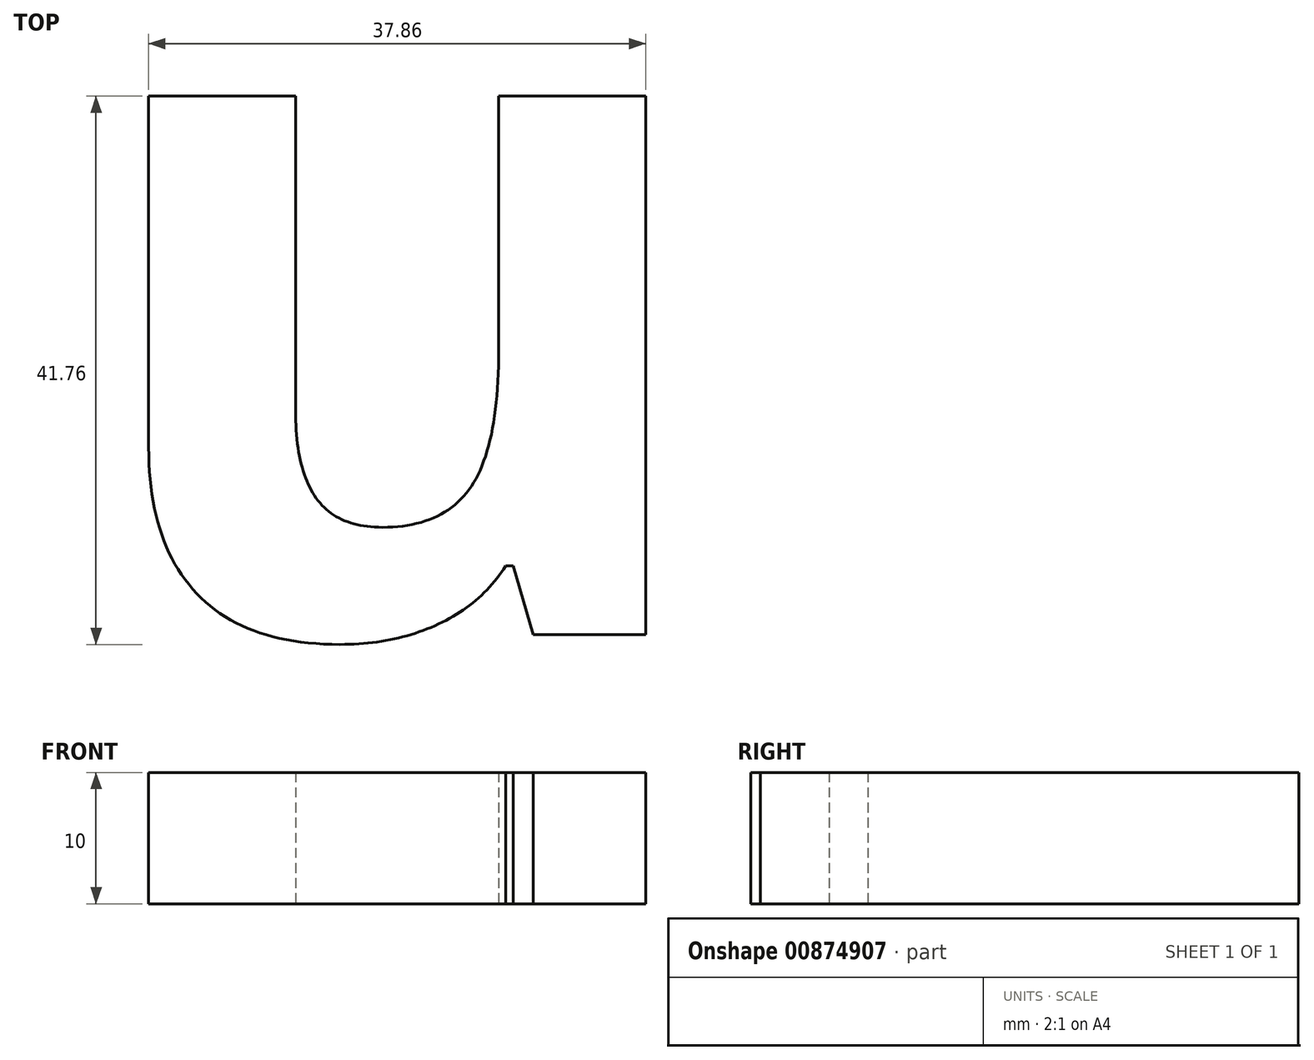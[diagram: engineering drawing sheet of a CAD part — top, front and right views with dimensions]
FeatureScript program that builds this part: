
annotation { "Feature Type Name" : "Feature", "Feature Type Description" : "" }
export const myFeature = defineFeature(function(context is Context, id is Id, definition is map)
    precondition{}
    {
        {
            var Q0;
            Q0=qCreatedBy(makeId("Top.planeOp"),FACE);
            var sketch = newSketch(context, id + "F0", { "sketchPlane" : qUnion([Q0])});
            skText(sketch, "E0", { "text": "u", "fontName": "OpenSans-Bold.ttf"});
            const initialGuessF0  = {"E0": [0, 0, 1, 0, 0.0541]};
            skSetInitialGuess(sketch, initialGuessF0);
            skSolve(sketch);
        }
        {
            var Q0;
            Q0 = qSketchRegion(id + "F0", true);
            extrude(context, id + "F1", {"entities" : qUnion([Q0]), "depth" : 10 * mm, "offsetDistance" : 25 * mm});
        }
    });
